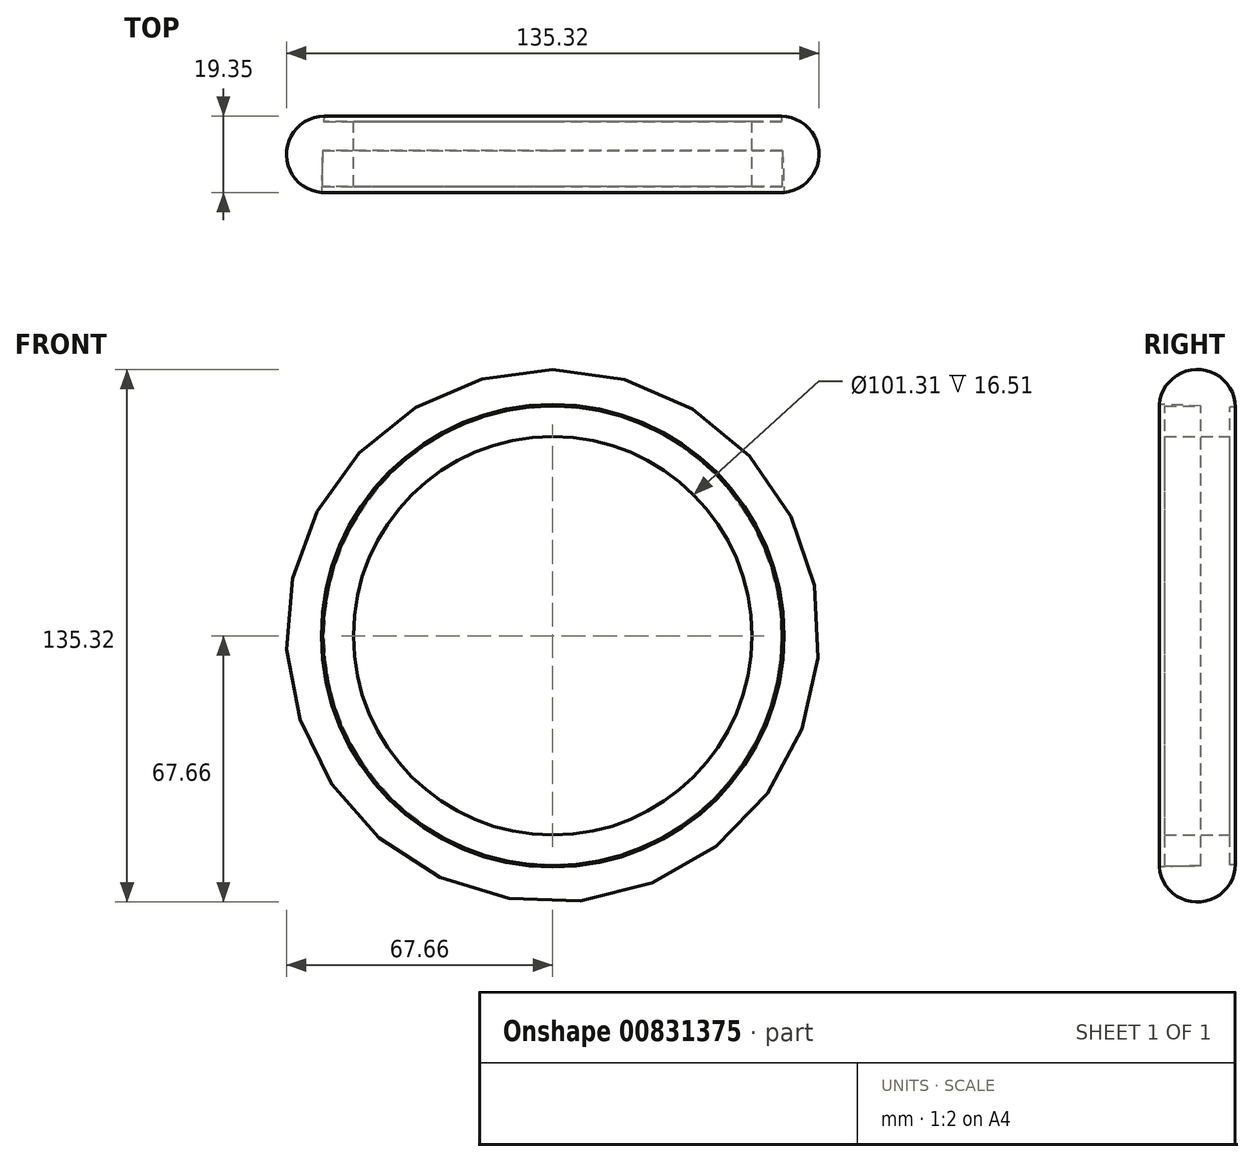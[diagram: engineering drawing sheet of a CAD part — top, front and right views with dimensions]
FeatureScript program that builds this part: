
annotation { "Feature Type Name" : "Feature", "Feature Type Description" : "" }
export const myFeature = defineFeature(function(context is Context, id is Id, definition is map)
    precondition{}
    {
        {
            var Q0;
            Q0=qCreatedBy(makeId("Front.planeOp"),FACE);
            var sketch = newSketch(context, id + "F0", { "sketchPlane" : qUnion([Q0])});
            skCircle(sketch, "E0", {"center": v(0, 0) * mm, "radius": 58.42 * mm});
            skLineSegment(sketch, "E1", {"start": v(0, 3.34) * mm, "end": v(-3.18, 3.34) * mm});
            skLineSegment(sketch, "E2", {"start": v(-3.18, 3.34) * mm, "end": v(-3.18, -3) * mm});
            skLineSegment(sketch, "E3", {"start": v(-3.17, -3) * mm, "end": v(3.18, -3) * mm});
            skLineSegment(sketch, "E4", {"start": v(3.18, -3) * mm, "end": v(3.18, 3.34) * mm});
            skLineSegment(sketch, "E5", {"start": v(3.18, 3.34) * mm, "end": v(0, 3.34) * mm});
            skPoint(sketch, "E6", {"position": v(3.18, 0.17) * mm});
            skPoint(sketch, "E7", {"position": v(0, -3) * mm});
            skPoint(sketch, "E8", {"position": v(-3.18, 0.17) * mm});
            skLineSegment(sketch, "E9", {"start": v(0, 3.34) * mm, "end": v(0, -3) * mm});
            skLineSegment(sketch, "E10", {"start": v(-3.18, 0.17) * mm, "end": v(3.18, 0.17) * mm});
            skCircle(sketch, "E11", {"center": v(0, 0) * mm, "radius": 50.65 * mm});
            skSolve(sketch);
        }
        {
            var Q0;
            Q0=qCreatedBy(makeId("Right.planeOp"),FACE);
            var sketch = newSketch(context, id + "F1", { "sketchPlane" : qUnion([Q0])});
            skArc(sketch, "E12", {"start": v(9.69, 58.13) * mm, "mid": v(0.32, 67.65) * mm, "end": v(-9.66, 58.77) * mm});
            skLineSegment(sketch, "E13", {"start": v(-9.66, 58.77) * mm, "end": v(9.69, 58.13) * mm});
            skLineSegment(sketch, "E14", {"start": v(0, 57.97) * mm, "end": v(0, 0) * mm});
            skLineSegment(sketch, "E15", {"start": v(-9.66, 58.77) * mm, "end": v(0, 57.97) * mm});
            skLineSegment(sketch, "E16", {"start": v(9.69, 58.13) * mm, "end": v(0, 57.97) * mm});
            skSolve(sketch);
        }
        {
            var Q0;
            Q0=qCreatedBy(makeId("Right.planeOp"),FACE);
            var sketch = newSketch(context, id + "F2", { "sketchPlane" : qUnion([Q0])});
            skLineSegment(sketch, "E17", {"start": v(0, 0) * mm, "end": v(3.8, 0) * mm});
            skLineSegment(sketch, "E18", {"start": v(3.8, 0) * mm, "end": v(-4.02, 0) * mm});
            skSolve(sketch);
        }
        {
            var Q0;
            Q0=makeQuery(id+"F1.imprint","IMPRINT",FACE,{"disambiguationData":[TD([[makeQuery(id+"F1.imprint","IMPRINT",EDGE,{"derivedFrom":sQuery(id+"F1.wireOp",EDGE,"E12")}),1.0]])]});
            var Q1;
            Q1=sQuery(id+"F2.wireOp",EDGE,"E18");
            revolve(context, id + "F3", {"surfaceOperationType" : NewSurfaceOperationType.NEW, "entities" : qUnion([Q0]), "axis" : qUnion([Q1]), "revolveType" : RevolveType.FULL});
        }
        {
            var Q0;
            Q0=makeQuery(id+"F0.imprint","IMPRINT",FACE,{"disambiguationData":[TD([[makeQuery(id+"F0.imprint","IMPRINT",EDGE,{"derivedFrom":sQuery(id+"F0.wireOp",EDGE,"E0")}),1.0]])]});
            extrude(context, id + "F4", {"entities" : qUnion([Q0]), "operationType" : NewBodyOperationType.ADD, "endBound" : BoundingType.SYMMETRIC, "depth" : 16.5 * mm, "offsetDistance" : 25.4 * mm});
        }
    });
